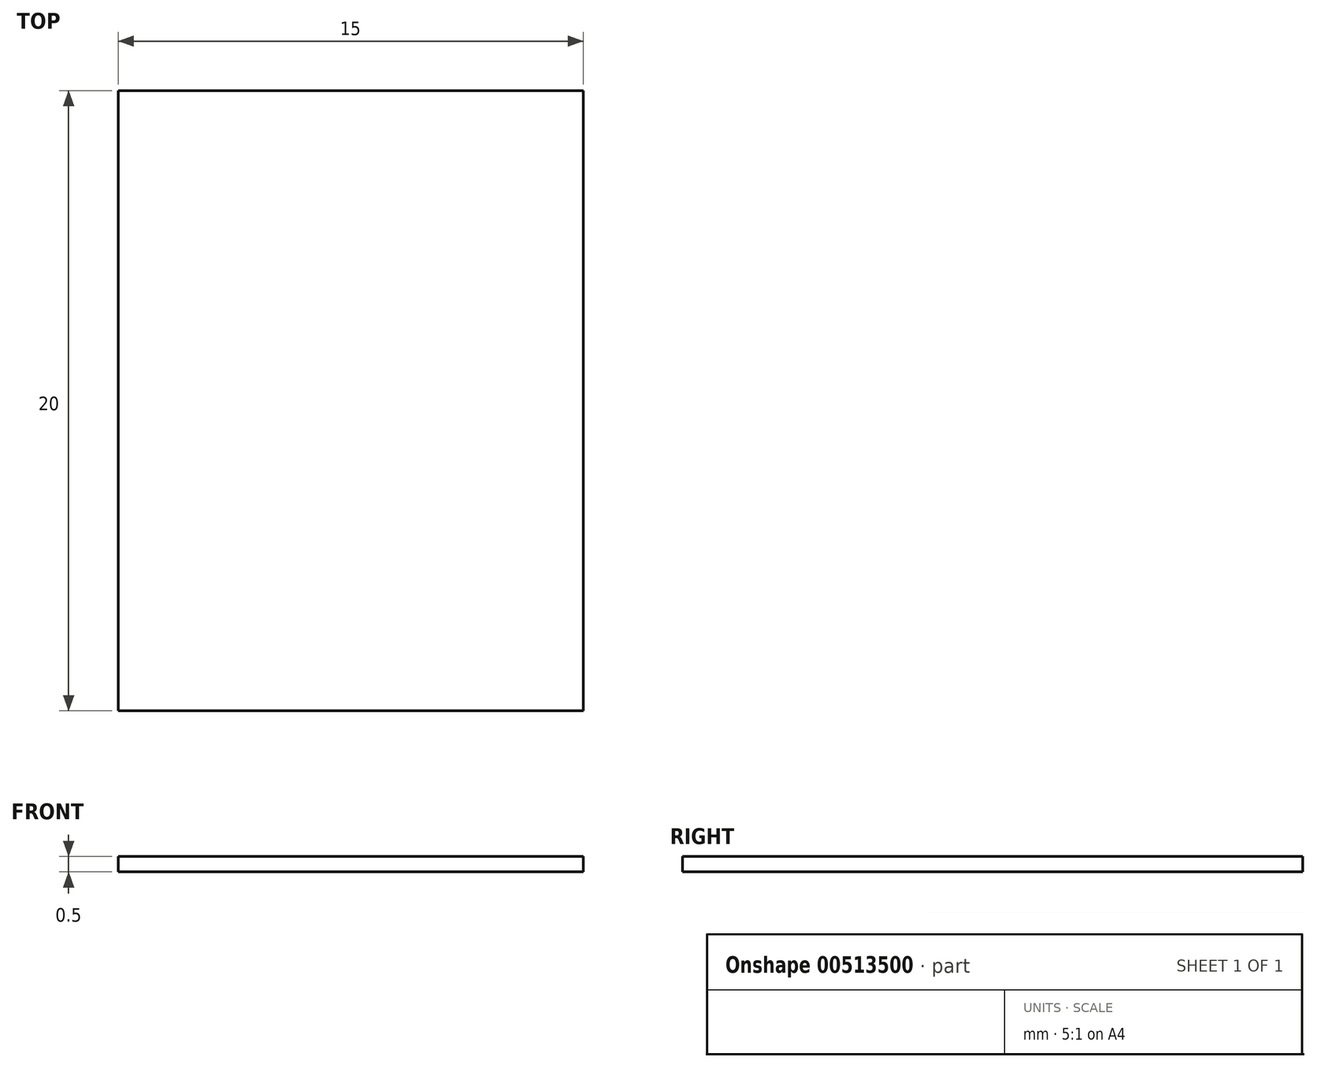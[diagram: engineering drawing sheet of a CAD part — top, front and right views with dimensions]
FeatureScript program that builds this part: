
annotation { "Feature Type Name" : "Feature", "Feature Type Description" : "" }
export const myFeature = defineFeature(function(context is Context, id is Id, definition is map)
    precondition{}
    {
        {
            var Q0;
            Q0=qCreatedBy(makeId("Top.planeOp"),FACE);
            var sketch = newSketch(context, id + "F0", { "sketchPlane" : qUnion([Q0])});
            skLineSegment(sketch, "E0.bottom", {"start": v(7.5, -10) * mm, "end": v(-7.5, -10) * mm});
            skLineSegment(sketch, "E0.top", {"start": v(7.5, 10) * mm, "end": v(-7.5, 10) * mm});
            skLineSegment(sketch, "E0.left", {"start": v(7.5, -10) * mm, "end": v(7.5, 10) * mm});
            skLineSegment(sketch, "E0.right", {"start": v(-7.5, -10) * mm, "end": v(-7.5, 10) * mm});
            skPoint(sketch, "E0.middle", {"position": v(0, 0) * mm});
            skSolve(sketch);
        }
        {
            var Q0;
            Q0=makeQuery(id+"F0.imprint","IMPRINT",FACE,{"disambiguationData":[TD([[makeQuery(id+"F0.imprint","IMPRINT",EDGE,{"derivedFrom":sQuery(id+"F0.wireOp",EDGE,"E0.bottom")}),-1.0]])]});
            extrude(context, id + "F1", {"entities" : qUnion([Q0]), "depth" : .5 * mm});
        }
    });
